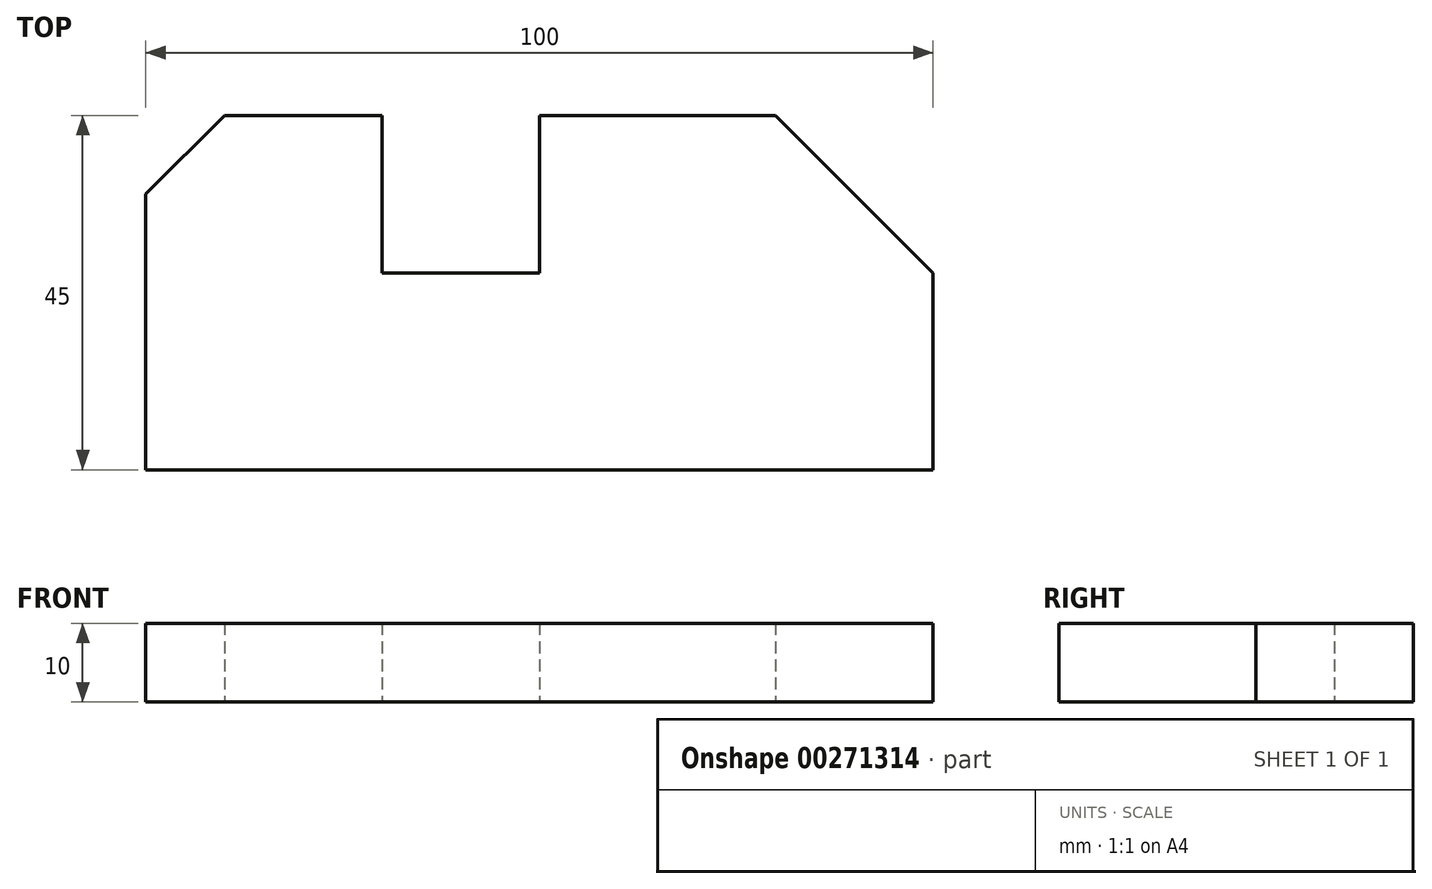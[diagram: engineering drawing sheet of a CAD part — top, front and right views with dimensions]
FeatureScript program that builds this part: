
annotation { "Feature Type Name" : "Feature", "Feature Type Description" : "" }
export const myFeature = defineFeature(function(context is Context, id is Id, definition is map)
    precondition{}
    {
        {
            var Q0;
            Q0=qCreatedBy(makeId("Top.planeOp"),FACE);
            var sketch = newSketch(context, id + "F0", { "sketchPlane" : qUnion([Q0])});
            skLineSegment(sketch, "E0.bottom", {"start": v(0, 0) * mm, "end": v(100, 0) * mm});
            skLineSegment(sketch, "E0.top", {"start": v(10, 45) * mm, "end": v(30, 45) * mm});
            skLineSegment(sketch, "E0.left", {"start": v(0, 0) * mm, "end": v(0, 35) * mm});
            skLineSegment(sketch, "E0.right", {"start": v(100, 0) * mm, "end": v(100, 25) * mm});
            skPoint(sketch, "E1", {"position": v(10, 45) * mm});
            skLineSegment(sketch, "E2", {"start": v(10, 45) * mm, "end": v(0, 35) * mm});
            skPoint(sketch, "E3", {"position": v(80, 45) * mm});
            skLineSegment(sketch, "E4", {"start": v(80, 45) * mm, "end": v(100, 25) * mm});
            skPoint(sketch, "E5", {"position": v(30, 45) * mm});
            skPoint(sketch, "E6", {"position": v(50, 45) * mm});
            skLineSegment(sketch, "E7", {"start": v(30, 45) * mm, "end": v(30, 25) * mm});
            skLineSegment(sketch, "E8", {"start": v(50, 45) * mm, "end": v(50, 25) * mm});
            skLineSegment(sketch, "E9", {"start": v(50, 25) * mm, "end": v(30, 25) * mm});
            skLineSegment(sketch, "E10.trimOffspring", {"start": v(50, 45) * mm, "end": v(80, 45) * mm});
            skSolve(sketch);
        }
        {
            var Q0;
            Q0 = qSketchRegion(id + "F0", true);
            extrude(context, id + "F1", {"entities" : qUnion([Q0]), "depth" : 10 * mm});
        }
    });
